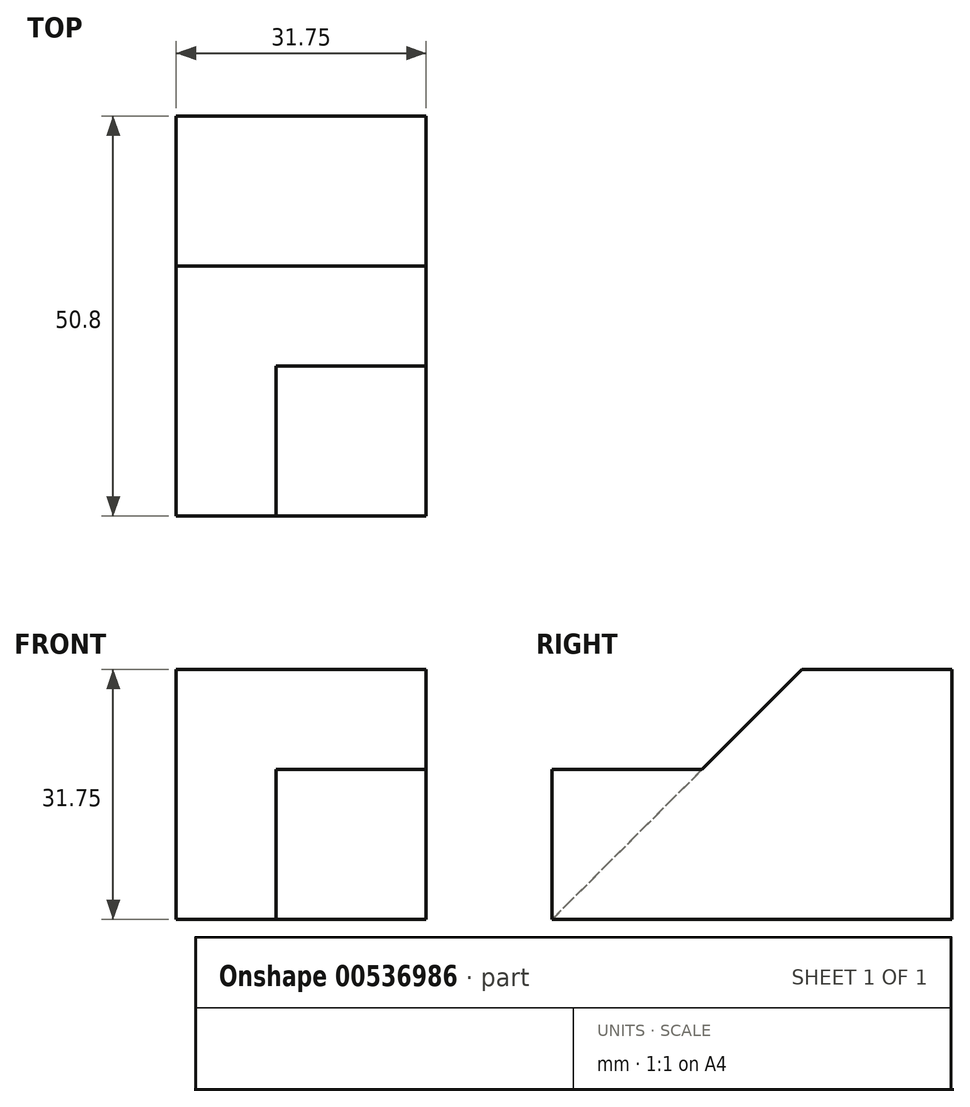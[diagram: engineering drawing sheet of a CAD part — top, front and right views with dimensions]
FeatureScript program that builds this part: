
annotation { "Feature Type Name" : "Feature", "Feature Type Description" : "" }
export const myFeature = defineFeature(function(context is Context, id is Id, definition is map)
    precondition{}
    {
        {
            var Q0;
            Q0=qCreatedBy(makeId("Front.planeOp"),FACE);
            var sketch = newSketch(context, id + "F0", { "sketchPlane" : qUnion([Q0])});
            skLineSegment(sketch, "E0", {"start": v(-58.8, 15.59) * mm, "end": v(-27.04, 15.59) * mm});
            skLineSegment(sketch, "E1", {"start": v(-27.04, 15.59) * mm, "end": v(-27.04, 47.34) * mm});
            skLineSegment(sketch, "E2", {"start": v(-27.04, 47.34) * mm, "end": v(-58.8, 47.34) * mm});
            skLineSegment(sketch, "E3", {"start": v(-58.8, 47.34) * mm, "end": v(-58.8, 15.59) * mm});
            skSolve(sketch);
        }
        {
            var Q0;
            Q0=makeQuery(id+"F0.imprint","IMPRINT",FACE,{"disambiguationData":[TD([[makeQuery(id+"F0.imprint","IMPRINT",EDGE,{"derivedFrom":sQuery(id+"F0.wireOp",EDGE,"E0")}),1.0]])]});
            extrude(context, id + "F1", {"entities" : qUnion([Q0]), "depth" : 50.8 * mm, "offsetDistance" : 25.4 * mm});
        }
        {
            var Q0;
            Q0=makeQuery(id+"F1.opExtrude","SWEPT_FACE",FACE,{"disambiguationData":[OSD([sQuery(id+"F0.wireOp",EDGE,"E3")])]});
            var sketch = newSketch(context, id + "F2", { "sketchPlane" : qUnion([Q0])});
            skLineSegment(sketch, "E4", {"start": v(19.05, 47.34) * mm, "end": v(50.8, 15.59) * mm});
            skSolve(sketch);
        }
        {
            var Q0;
            {var subQ0=sQuery(id+"F2.wireOp",EDGE,"E4");Q0=makeQuery(id+"F2.imprint","IMPRINT",FACE,{"disambiguationData":[TD([[makeQuery(id+"F2.imprint","IMPRINT",EDGE,{"derivedFrom":subQ0}),1.0]])]});}
            extrude(context, id + "F3", {"entities" : qUnion([Q0]), "operationType" : NewBodyOperationType.REMOVE, "oppositeDirection" : true, "depth" : 12.7 * mm, "offsetDistance" : 25.4 * mm});
        }
        {
            var Q0;
            Q0=makeQuery(id+"F3.boolean.opBoolean","COPY",FACE,{"derivedFrom":makeQuery(id+"F3.opExtrude","CAP_FACE",FACE,{"disambiguationData":[OSD([sQuery(id+"F0.wireOp",EDGE,"E2"),sQuery(id+"F0.wireOp",EDGE,"E3"),sQuery(id+"F2.wireOp",EDGE,"E4")])],"isStart":false})});
            var sketch = newSketch(context, id + "F4", { "sketchPlane" : qUnion([Q0])});
            skLineSegment(sketch, "E5", {"start": v(31.75, 34.64) * mm, "end": v(50.8, 34.64) * mm});
            skSolve(sketch);
        }
        {
            var Q0;
            {var subQ0=sQuery(id+"F4.wireOp",EDGE,"E5");Q0=makeQuery(id+"F4.imprint","IMPRINT",FACE,{"disambiguationData":[TD([[makeQuery(id+"F4.imprint","IMPRINT",EDGE,{"derivedFrom":subQ0}),1.0]])]});}
            extrude(context, id + "F5", {"entities" : qUnion([Q0]), "operationType" : NewBodyOperationType.REMOVE, "endBound" : BoundingType.THROUGH_ALL, "oppositeDirection" : true, "depth" : 25.4 * mm, "offsetDistance" : 25.4 * mm});
        }
    });
